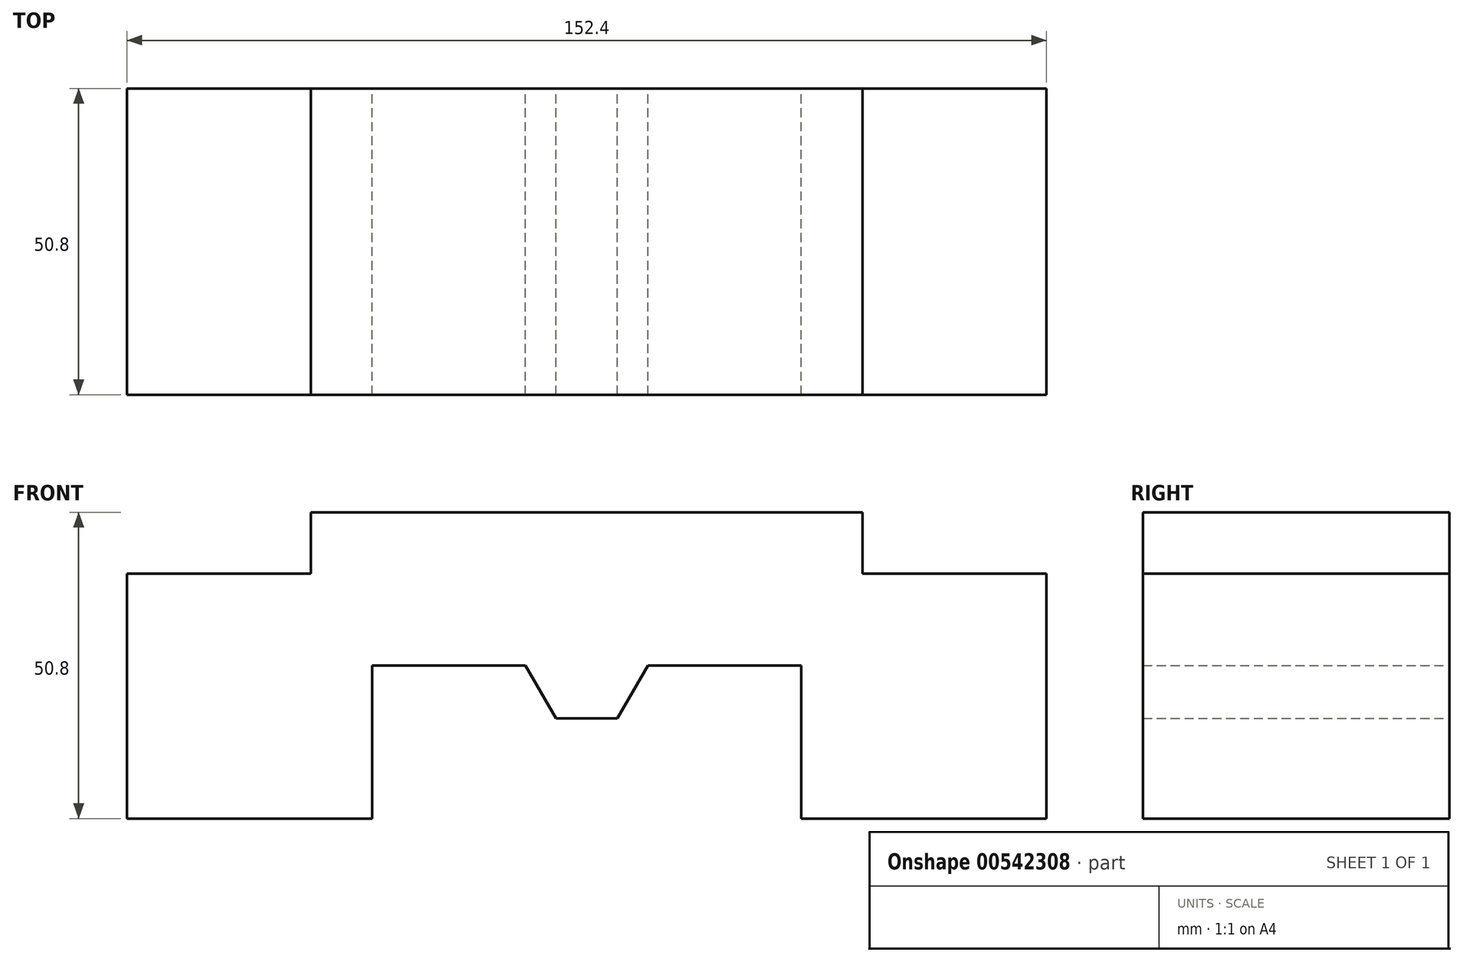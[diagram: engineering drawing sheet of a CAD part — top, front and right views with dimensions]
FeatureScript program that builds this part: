
annotation { "Feature Type Name" : "Feature", "Feature Type Description" : "" }
export const myFeature = defineFeature(function(context is Context, id is Id, definition is map)
    precondition{}
    {
        {
            var Q0;
            Q0=qCreatedBy(makeId("Front.planeOp"),FACE);
            var sketch = newSketch(context, id + "F0", { "sketchPlane" : qUnion([Q0])});
            skLineSegment(sketch, "E0", {"start": v(0, 38.3) * mm, "end": v(45.72, 38.3) * mm});
            skLineSegment(sketch, "E1", {"start": v(45.72, 38.3) * mm, "end": v(45.72, 28.15) * mm});
            skLineSegment(sketch, "E2", {"start": v(45.72, 28.15) * mm, "end": v(76.2, 28.15) * mm});
            skLineSegment(sketch, "E3", {"start": v(76.2, 28.15) * mm, "end": v(76.2, -12.5) * mm});
            skLineSegment(sketch, "E4", {"start": v(76.2, -12.5) * mm, "end": v(35.56, -12.5) * mm});
            skLineSegment(sketch, "E5", {"start": v(35.56, -12.5) * mm, "end": v(35.56, 12.9) * mm});
            skLineSegment(sketch, "E6", {"start": v(35.56, 12.9) * mm, "end": v(10.16, 12.9) * mm});
            skLineSegment(sketch, "E7", {"start": v(10.16, 12.9) * mm, "end": v(5.08, 4.11) * mm});
            skLineSegment(sketch, "E8", {"start": v(5.08, 4.11) * mm, "end": v(0, 4.11) * mm});
            skLineSegment(sketch, "E9", {"start": v(0, 38.3) * mm, "end": v(-45.72, 38.3) * mm});
            skLineSegment(sketch, "E10", {"start": v(-45.72, 38.3) * mm, "end": v(-45.72, 28.15) * mm});
            skLineSegment(sketch, "E11", {"start": v(-45.72, 28.15) * mm, "end": v(-76.2, 28.15) * mm});
            skLineSegment(sketch, "E12", {"start": v(-76.2, 28.15) * mm, "end": v(-76.2, -12.5) * mm});
            skLineSegment(sketch, "E13", {"start": v(-76.2, -12.5) * mm, "end": v(-35.56, -12.5) * mm});
            skLineSegment(sketch, "E14", {"start": v(-35.56, -12.5) * mm, "end": v(-35.56, 12.9) * mm});
            skLineSegment(sketch, "E15", {"start": v(-35.56, 12.9) * mm, "end": v(-10.16, 12.9) * mm});
            skLineSegment(sketch, "E16", {"start": v(0, 4.11) * mm, "end": v(-5.08, 4.11) * mm});
            skLineSegment(sketch, "E17", {"start": v(-5.08, 4.11) * mm, "end": v(-10.16, 12.9) * mm});
            skSolve(sketch);
        }
        {
            var Q0;
            Q0=qCreatedBy(makeId("Top.planeOp"),FACE);
            var sketch = newSketch(context, id + "F1", { "sketchPlane" : qUnion([Q0])});
            skLineSegment(sketch, "E18", {"start": v(76.2, 0) * mm, "end": v(76.2, -50.8) * mm});
            skLineSegment(sketch, "E19", {"start": v(76.2, -50.8) * mm, "end": v(-76.2, -50.8) * mm});
            skLineSegment(sketch, "E20", {"start": v(-76.2, -50.8) * mm, "end": v(-76.2, 0) * mm});
            skLineSegment(sketch, "E21", {"start": v(-76.2, 0) * mm, "end": v(76.2, 0) * mm});
            skPoint(sketch, "E22", {"position": v(76.2, -25.4) * mm});
            skPoint(sketch, "E23", {"position": v(-76.2, -25.4) * mm});
            skPoint(sketch, "E24", {"position": v(60.96, -50.8) * mm});
            skPoint(sketch, "E25", {"position": v(-60.96, -50.8) * mm});
            skCircle(sketch, "E26", {"center": v(60.96, -25.4) * mm, "radius": 8.9 * mm});
            skCircle(sketch, "E27", {"center": v(-60.96, -25.4) * mm, "radius": 8.9 * mm});
            skSolve(sketch);
        }
        {
            var Q0;
            Q0=makeQuery(id+"F0.imprint","IMPRINT",FACE,{"disambiguationData":[TD([[makeQuery(id+"F0.imprint","IMPRINT",EDGE,{"derivedFrom":sQuery(id+"F0.wireOp",EDGE,"E0")}),-1.0]])]});
            extrude(context, id + "F2", {"entities" : qUnion([Q0]), "depth" : 50.8 * mm, "offsetDistance" : 25.4 * mm});
        }
    });
